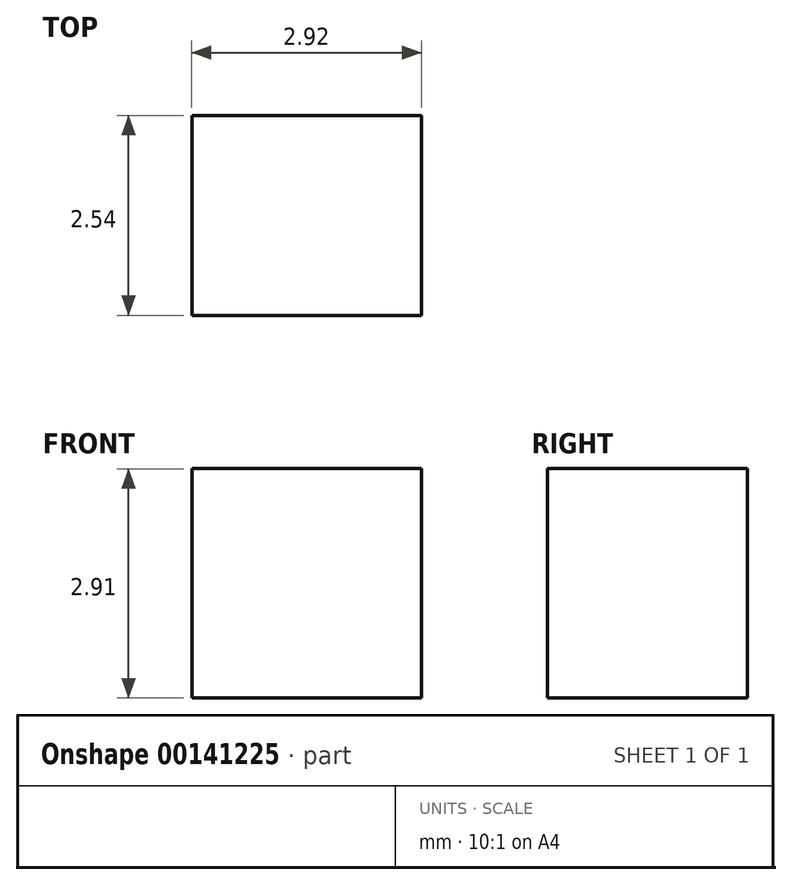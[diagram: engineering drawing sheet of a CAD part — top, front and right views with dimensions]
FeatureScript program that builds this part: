
annotation { "Feature Type Name" : "Feature", "Feature Type Description" : "" }
export const myFeature = defineFeature(function(context is Context, id is Id, definition is map)
    precondition{}
    {
        {
            var Q0;
            Q0=qCreatedBy(makeId("Front.planeOp"),FACE);
            var sketch = newSketch(context, id + "F0", { "sketchPlane" : qUnion([Q0])});
            skLineSegment(sketch, "E0.bottom", {"start": v(-54.1, 24.3) * mm, "end": v(-51.18, 24.3) * mm});
            skLineSegment(sketch, "E0.top", {"start": v(-54.1, 21.38) * mm, "end": v(-51.18, 21.38) * mm});
            skLineSegment(sketch, "E0.left", {"start": v(-54.1, 24.3) * mm, "end": v(-54.1, 21.38) * mm});
            skLineSegment(sketch, "E0.right", {"start": v(-51.18, 24.3) * mm, "end": v(-51.18, 21.38) * mm});
            skSolve(sketch);
        }
        {
            var Q0;
            Q0 = qSketchRegion(id + "F0", true);
            extrude(context, id + "F1", {"entities" : qUnion([Q0]), "depth" : 2.54 * mm});
        }
    });
